# Revit family: DEEP FOCUS ROUND LIGHT
name_source: partatom
category: Lighting Fixtures
units: mm (PartAtom-declared; Revit-internal decimal feet)

## family parameters
Cut with Voids When Loaded = No
Host = Face
Light Source = Yes
Part Type = Normal
Room Calculation Point = No
Round Connector Dimension = Use Diameter
Shared = No

## types (12) — shared parameters
Average life based on 77F(HRS) = 50000
B = 0' - 3 1/2"
B1 = 0' - 0"
B2 = 0' - 0"
CRI = 90
Canopy Dia = 0' - 0"
Canopy Height = 0' - 0"
Color Filter = 16777215
Default Elevation = 0' - 0"
Description = The Deep Focus Round Light offers the FOCUS family more choices. Fixture comes in diameters 
from 11.8 through 23.6 Deep recessed light source design achieving perfect glare control.
Dimming / Control = 0-10 V
Dimming Lamp Color Temperature Shift = <None>
Fixture Height = 3' - 0"
IP Rating = 20
Inside Element = White
Load Classification = Lighting
Manufacturer = Above All Lighting
Power Factor = 1
Suspender Material = Aluminum
Tilt Angle = -90.00°
Type Comments = DEEP FOCUS ROUND LIGHT
URL = https://www.abovealllighting.com
Voltage = 120-277 V

## per-type parameters (varying)
| type | Aircraft Cable Pendant Mount | Apparent Load | D1 | D2 | Finish/Color | Fixture Diameter | Order number | Photometric Web File | Surface Mount | Wattage Comments |
| DFRD12-15-40901-ACPMK | Yes | 19 VA | 0' - 5 29/32" | 0' - 4 13/32" | White-PMMA Aluminum | 0' - 11 13/16" | 16821 | DFRD12_15_40901_ACPMK.IES | No | 15 W |
| DFRD16-20-40901-ACPMK | Yes | 25 VA | 0' - 7 27/32" | 0' - 6 11/32" | White-PMMA Aluminum | 1' - 3 23/32" | 16822 | DFRD16_20_XX901.IES | No | 20 W |
| DFRD19-25-40901-ACPMK | Yes | 31 VA | 0' - 9 7/16" | 0' - 7 15/16" | White-PMMA Aluminum | 1' - 6 29/32" | 16823 | DFRD19_25_XX901.IES | No | 25 W |
| DFRD24-40-40901-ACPMK | Yes | 50 VA | 0' - 11 13/16" | 0' - 10 5/16" | White | 1' - 11 19/32" | 16824 | DFRD24_40_XX901.IES | No | 40 W |
| DFRID19-50-40901-ACPMK | Yes | 63 VA | 0' - 9 7/16" | 0' - 7 15/16" | White-PMMA Aluminum | 1' - 6 29/32" | 16825 | DFRID19_50_XX901.IES | No | 50 W |
| DFRID24-80-40901-ACPMK | Yes | 100 VA | 0' - 11 13/16" | 0' - 10 5/16" | White-PMMA Aluminum | 1' - 11 19/32" | 16826 | DFRID24_80_XX901.IES | No | 80 W |
| DFRD12-15-40901-SMK | No | 19 VA | 0' - 5 29/32" | 0' - 4 13/32" | White-PMMA Aluminum | 0' - 11 13/16" | 16827 | DFRD12_15_XX901.IES | Yes | 15 W |
| DFRD16-20-40901-SMK | No | 25 VA | 0' - 7 27/32" | 0' - 6 11/32" | White-PMMA Aluminum | 1' - 3 23/32" | 16828 | DFRD16_20_XX901.IES | Yes | 20 W |
| DFRD19-25-40901-SMK | No | 31 VA | 0' - 9 7/16" | 0' - 7 15/16" | White-PMMA Aluminum | 1' - 6 29/32" | 16829 | DFRD19_25_XX901.IES | Yes | 25 W |
| DFRD24-40-40901-SMK | No | 50 VA | 0' - 11 13/16" | 0' - 10 5/16" | White-PMMA Aluminum | 1' - 11 19/32" | 16830 | DFRD24_40_XX901.IES | Yes | 40 W |
| DFRID19-50-40901-SMK | No | 63 VA | 0' - 9 7/16" | 0' - 7 15/16" | White-PMMA Aluminum | 1' - 6 29/32" | 16831 | DFRID19_50_XX901.IES | Yes | 50 W |
| DFRID24-80-40901-SMK | No | 100 VA | 0' - 11 13/16" | 0' - 10 5/16" | White-PMMA Aluminum | 1' - 11 19/32" | 16832 | DFRID24_80_XX901.IES | Yes | 80 W |

note: column(s) folded — value = type name in every type: Model

## geometry (parser evidence)
native form markers: Sweep x18
no freeform markers — native parametric forms only
